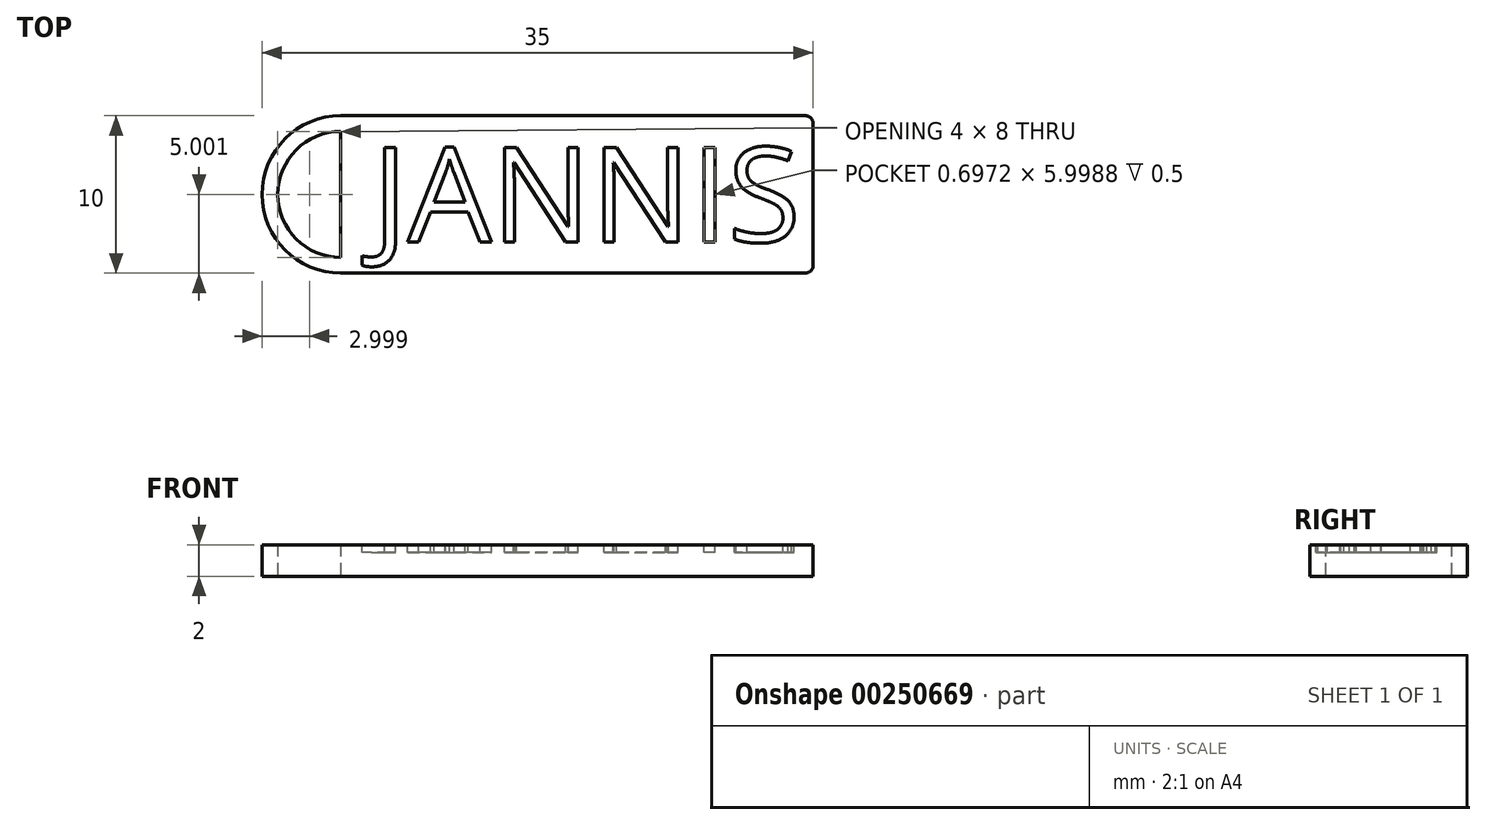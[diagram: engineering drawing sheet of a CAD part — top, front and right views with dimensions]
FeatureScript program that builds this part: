
annotation { "Feature Type Name" : "Feature", "Feature Type Description" : "" }
export const myFeature = defineFeature(function(context is Context, id is Id, definition is map)
    precondition{}
    {
        {
            var Q0;
            Q0=qCreatedBy(makeId("Top.planeOp"),FACE);
            var sketch = newSketch(context, id + "F0", { "sketchPlane" : qUnion([Q0])});
            skLineSegment(sketch, "E0.bottom", {"start": v(-5.27, 3.22) * mm, "end": v(24.73, 3.22) * mm});
            skLineSegment(sketch, "E0.top", {"start": v(-5.27, -6.78) * mm, "end": v(24.73, -6.78) * mm});
            skLineSegment(sketch, "E0.left", {"start": v(-5.27, 3.22) * mm, "end": v(-5.27, -6.78) * mm});
            skLineSegment(sketch, "E0.right", {"start": v(24.73, 3.22) * mm, "end": v(24.73, -6.78) * mm});
            skArc(sketch, "E1", {"start": v(-5.27, 3.22) * mm, "mid": v(-10.27, -1.78) * mm, "end": v(-5.27, -6.78) * mm});
            skArc(sketch, "E2", {"start": v(-5.27, 2.22) * mm, "mid": v(-9.27, -1.78) * mm, "end": v(-5.27, -5.78) * mm});
            skSolve(sketch);
        }
        {
            var Q0;
            Q0=qSketchRegion(id+"F0",true);
            extrude(context, id + "F4", {"entities" : qUnion([Q0]), "depth" : 2 * mm});
        }
        {
            var Q0;
            Q0=makeQuery(id+"F4.opExtrude","SWEPT_EDGE",EDGE,{"disambiguationData":[OSD([sQuery(id+"F0.wireOp",EDGE,"E0.top"),sQuery(id+"F0.wireOp",EDGE,"E0.right")])]});
            var Q1;
            Q1=makeQuery(id+"F4.opExtrude","SWEPT_EDGE",EDGE,{"disambiguationData":[OSD([sQuery(id+"F0.wireOp",EDGE,"E0.bottom"),sQuery(id+"F0.wireOp",EDGE,"E0.right")])]});
            fillet(context, id + "F1", {"entities" : qUnion([Q0, Q1]), "radius" : 0.5 * mm, "tangentPropagation" : true, "allowEdgeOverflow" : false});
        }
        {
            var Q0;
            Q0=makeQuery(id+"F4.opExtrude","CAP_FACE",FACE,{"disambiguationData":[OSD([sQuery(id+"F0.wireOp",EDGE,"E0.bottom"),sQuery(id+"F0.wireOp",EDGE,"E0.top"),sQuery(id+"F0.wireOp",EDGE,"E0.left"),sQuery(id+"F0.wireOp",EDGE,"E0.right"),sQuery(id+"F0.wireOp",EDGE,"E1"),sQuery(id+"F0.wireOp",EDGE,"E2")])],"isStart":false});
            var sketch = newSketch(context, id + "F2", { "sketchPlane" : qUnion([Q0])});
            skText(sketch, "E3", { "text": "JANNIS", "fontName": "OpenSans-Regular.ttf"});
            skPoint(sketch, "E4", {"position": v(-3.27, -1.78) * mm});
            skPoint(sketch, "E5", {"position": v(24.73, -1.78) * mm});
            skPoint(sketch, "E6.positionSnap0", {"position": v(-5.27, -1.78) * mm});
            const initialGuessF2  = {"E3": [-0.00327, -0.0048, 1, 0, 0.00605]};
            skSetInitialGuess(sketch, initialGuessF2);
            skSolve(sketch);
        }
        {
            var Q0;
            Q0 = qSketchRegion(id + "F2", true);
            extrude(context, id + "F3", {"entities" : qUnion([Q0]), "operationType" : NewBodyOperationType.REMOVE, "oppositeDirection" : true, "depth" : 0.5 * mm});
        }
    });
